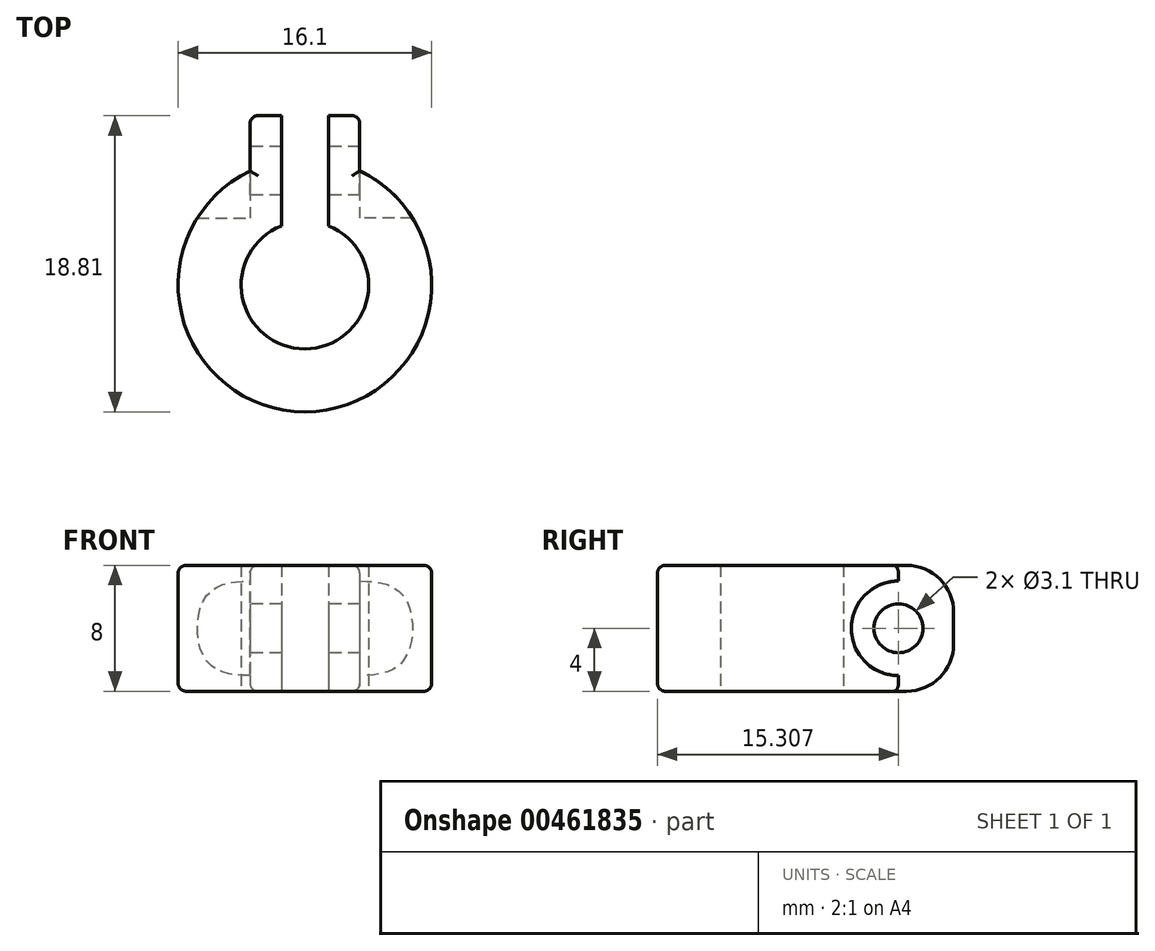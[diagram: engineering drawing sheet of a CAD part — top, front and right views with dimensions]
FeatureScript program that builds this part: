
annotation { "Feature Type Name" : "Feature", "Feature Type Description" : "" }
export const myFeature = defineFeature(function(context is Context, id is Id, definition is map)
    precondition{}
    {
        {
            var Q0;
            Q0=qCreatedBy(makeId("Top.planeOp"),FACE);
            var sketch = newSketch(context, id + "F0", { "sketchPlane" : qUnion([Q0])});
            skArc(sketch, "E0", {"start": v(-1.5, 3.76) * mm, "mid": v(0, -4.05) * mm, "end": v(1.5, 3.76) * mm});
            skArc(sketch, "E1.0", {"start": v(-3.48, 7.26) * mm, "mid": v(0, -8.05) * mm, "end": v(3.48, 7.26) * mm});
            skLineSegment(sketch, "E2.left", {"start": v(1.5, 7.9) * mm, "end": v(1.5, 3.76) * mm});
            skLineSegment(sketch, "E2.right", {"start": v(-1.5, 7.9) * mm, "end": v(-1.5, 3.76) * mm});
            skLineSegment(sketch, "E3.top", {"start": v(-1.5, 9.76) * mm, "end": v(-3.48, 9.76) * mm});
            skLineSegment(sketch, "E3.left", {"start": v(-1.5, 3.76) * mm, "end": v(-1.5, 9.76) * mm});
            skLineSegment(sketch, "E3.right", {"start": v(-3.48, 7.26) * mm, "end": v(-3.48, 9.76) * mm});
            skLineSegment(sketch, "E4.MirrorCS", {"start": v(1.5, 9.76) * mm, "end": v(3.48, 9.76) * mm});
            skLineSegment(sketch, "E5.MirrorCS", {"start": v(3.48, 7.26) * mm, "end": v(3.48, 9.76) * mm});
            skLineSegment(sketch, "E6.MirrorCS", {"start": v(1.5, 3.76) * mm, "end": v(1.5, 9.76) * mm});
            skSolve(sketch);
        }
        {
            var Q0;
            Q0=qSketchRegion(id+"F0",true);
            extrude(context, id + "F1", {"entities" : qUnion([Q0]), "depth" : 8 * mm});
        }
        {
            var Q0;
            Q0=qCreatedBy(makeId("Right.planeOp"),FACE);
            var sketch = newSketch(context, id + "F2", { "sketchPlane" : qUnion([Q0])});
            skCircle(sketch, "E7", {"center": v(7.26, 4) * mm, "radius": 1.55 * mm});
            skSolve(sketch);
        }
        {
            var Q0;
            Q0=qSketchRegion(id+"F2",true);
            extrude(context, id + "F3", {"entities" : qUnion([Q0]), "operationType" : NewBodyOperationType.REMOVE, "endBound" : BoundingType.SYMMETRIC, "depth" : 25 * mm});
        }
        {
            var Q0;
            Q0=makeQuery(id+"F1.opExtrude","SWEPT_FACE",FACE,{"disambiguationData":[OSD([sQuery(id+"F0.wireOp",EDGE,"E4.MirrorCS")])]});
            var Q1;
            Q1=makeQuery(id+"F1.opExtrude","SWEPT_FACE",FACE,{"disambiguationData":[OSD([sQuery(id+"F0.wireOp",EDGE,"E3.top")])]});
            extrude(context, id + "F4", {"entities" : qUnion([Q0, Q1]), "operationType" : NewBodyOperationType.ADD, "depth" : 1 * mm});
        }
        {
            var Q0;
            {var subQ0=sQuery(id+"F0.wireOp",EDGE,"E5.MirrorCS");Q0=makeQuery(id+"F4.boolean.opBoolean","MERGE",FACE,{"derivedFrom":[makeQuery(id+"F1.opExtrude","SWEPT_FACE",FACE,{"disambiguationData":[OSD([subQ0])]}),makeQuery(id+"F4.opExtrude","SWEPT_FACE",FACE,{"disambiguationData":[OSD([sQuery(id+"F0.wireOp",EDGE,"E4.MirrorCS"),subQ0])]})]});}
            var sketch = newSketch(context, id + "F5", { "sketchPlane" : qUnion([Q0])});
            skPoint(sketch, "E8.0", {"position": v(7.26, 4) * mm});
            skCircle(sketch, "E9", {"center": v(7.26, 4) * mm, "radius": 3 * mm});
            skSolve(sketch);
        }
        {
            var Q0;
            {var subQ2=sQuery(id+"F0.wireOp",EDGE,"E5.MirrorCS");var subQ9=makeQuery(id+"F3.opExtrude","SWEPT_FACE",FACE,{"disambiguationData":[OSD([sQuery(id+"F2.wireOp",EDGE,"E7")])]});var subQ11=makeQuery(id+"F1.opExtrude","SWEPT_FACE",FACE,{"disambiguationData":[OSD([subQ2])]});var subQ17=makeQuery(id+"F3.boolean.opBoolean","INTERSECT",EDGE,{"derivedFrom":[subQ11,subQ9]});Q0=makeQuery(id+"F5.imprint","IMPRINT",FACE,{"disambiguationData":[TD([[makeQuery(id+"F5.imprint","IMPRINT",EDGE,{"derivedFrom":subQ17}),1.0]])]});}
            extrude(context, id + "F6", {"entities" : qUnion([Q0]), "operationType" : NewBodyOperationType.REMOVE, "depth" : 25 * mm});
        }
        {
            var Q0;
            {var subQ0=sQuery(id+"F0.wireOp",EDGE,"E3.right");Q0=makeQuery(id+"F4.boolean.opBoolean","MERGE",FACE,{"derivedFrom":[makeQuery(id+"F1.opExtrude","SWEPT_FACE",FACE,{"disambiguationData":[OSD([subQ0])]}),makeQuery(id+"F4.opExtrude","SWEPT_FACE",FACE,{"disambiguationData":[OSD([sQuery(id+"F0.wireOp",EDGE,"E3.top"),subQ0])]})]});}
            var sketch = newSketch(context, id + "F7", { "sketchPlane" : qUnion([Q0])});
            skPoint(sketch, "E10.0", {"position": v(-7.26, 4) * mm});
            skCircle(sketch, "E11", {"center": v(-7.26, 4) * mm, "radius": 3 * mm});
            skSolve(sketch);
        }
        {
            var Q0;
            {var subQ4=sQuery(id+"F0.wireOp",EDGE,"E3.right");var subQ9=makeQuery(id+"F3.opExtrude","SWEPT_FACE",FACE,{"disambiguationData":[OSD([sQuery(id+"F2.wireOp",EDGE,"E7")])]});var subQ11=makeQuery(id+"F1.opExtrude","SWEPT_FACE",FACE,{"disambiguationData":[OSD([subQ4])]});var subQ17=makeQuery(id+"F3.boolean.opBoolean","INTERSECT",EDGE,{"derivedFrom":[subQ11,subQ9]});Q0=makeQuery(id+"F7.imprint","IMPRINT",FACE,{"disambiguationData":[TD([[makeQuery(id+"F7.imprint","IMPRINT",EDGE,{"derivedFrom":subQ17}),-1.0]])]});}
            extrude(context, id + "F8", {"entities" : qUnion([Q0]), "operationType" : NewBodyOperationType.REMOVE, "depth" : 25 * mm});
        }
        {
            var Q0;
            {var subQ0=sQuery(id+"F0.wireOp",EDGE,"E4.MirrorCS");Q0=makeQuery(id+"F4.opExtrude","CAP_EDGE",EDGE,{"disambiguationData":[OSD([subQ0]),TDD([makeQuery(id+"F1.opExtrude","CAP_EDGE",EDGE,{"disambiguationData":[OSD([subQ0])],"isStart":false})])],"isStart":false});}
            var Q1;
            {var subQ0=sQuery(id+"F0.wireOp",EDGE,"E4.MirrorCS");Q1=makeQuery(id+"F4.opExtrude","CAP_EDGE",EDGE,{"disambiguationData":[OSD([subQ0]),TDD([makeQuery(id+"F1.opExtrude","CAP_EDGE",EDGE,{"disambiguationData":[OSD([subQ0])],"isStart":true})])],"isStart":false});}
            fillet(context, id + "F9", {"entities" : qUnion([Q0, Q1]), "radius" : 3 * mm, "tangentPropagation" : true, "allowEdgeOverflow" : false});
        }
        {
            var Q0;
            {var subQ0=sQuery(id+"F0.wireOp",EDGE,"E3.top");Q0=makeQuery(id+"F4.opExtrude","CAP_EDGE",EDGE,{"disambiguationData":[OSD([subQ0]),TDD([makeQuery(id+"F1.opExtrude","CAP_EDGE",EDGE,{"disambiguationData":[OSD([subQ0])],"isStart":false})])],"isStart":false});}
            var Q1;
            {var subQ0=sQuery(id+"F0.wireOp",EDGE,"E3.top");Q1=makeQuery(id+"F4.opExtrude","CAP_EDGE",EDGE,{"disambiguationData":[OSD([subQ0]),TDD([makeQuery(id+"F1.opExtrude","CAP_EDGE",EDGE,{"disambiguationData":[OSD([subQ0])],"isStart":true})])],"isStart":false});}
            fillet(context, id + "F10", {"entities" : qUnion([Q0, Q1]), "radius" : 3 * mm, "tangentPropagation" : true, "allowEdgeOverflow" : false});
        }
        {
            var Q0;
            {var subQ0=sQuery(id+"F0.wireOp",EDGE,"E3.right");var subQ1=sQuery(id+"F0.wireOp",EDGE,"E3.top");Q0=makeQuery(id+"F10.opFillet","BLEND_EDGE",EDGE,{"blendedFrom":[makeQuery(id+"F4.opExtrude","CAP_EDGE",EDGE,{"disambiguationData":[OSD([subQ1]),TDD([makeQuery(id+"F1.opExtrude","CAP_EDGE",EDGE,{"disambiguationData":[OSD([subQ1])],"isStart":false})])],"isStart":false}),makeQuery(id+"F8.boolean.opBoolean","MERGE",FACE,{"derivedFrom":[makeQuery(id+"F4.boolean.opBoolean","MERGE",FACE,{"derivedFrom":[makeQuery(id+"F1.opExtrude","SWEPT_FACE",FACE,{"disambiguationData":[OSD([subQ0])]}),makeQuery(id+"F4.opExtrude","SWEPT_FACE",FACE,{"disambiguationData":[OSD([subQ1,subQ0])]})]}),makeQuery(id+"F8.opExtrude","CAP_FACE",FACE,{"disambiguationData":[OSD([sQuery(id+"F0.wireOp",EDGE,"E1.0"),subQ0,sQuery(id+"F2.wireOp",EDGE,"E7"),sQuery(id+"F7.wireOp",EDGE,"E11")])],"isStart":true})]})],"blendedInto":[makeQuery(id+"F8.boolean.opBoolean","MERGE",FACE,{"derivedFrom":[makeQuery(id+"F4.boolean.opBoolean","MERGE",FACE,{"derivedFrom":[makeQuery(id+"F1.opExtrude","SWEPT_FACE",FACE,{"disambiguationData":[OSD([subQ0])]}),makeQuery(id+"F4.opExtrude","SWEPT_FACE",FACE,{"disambiguationData":[OSD([subQ1,subQ0])]})]}),makeQuery(id+"F8.opExtrude","CAP_FACE",FACE,{"disambiguationData":[OSD([sQuery(id+"F0.wireOp",EDGE,"E1.0"),subQ0,sQuery(id+"F2.wireOp",EDGE,"E7"),sQuery(id+"F7.wireOp",EDGE,"E11")])],"isStart":true})]})]});}
            var Q1;
            {var subQ0=sQuery(id+"F0.wireOp",EDGE,"E3.right");var subQ1=sQuery(id+"F0.wireOp",EDGE,"E3.top");Q1=makeQuery(id+"F4.boolean.opBoolean","MERGE",EDGE,{"derivedFrom":[makeQuery(id+"F1.opExtrude","CAP_EDGE",EDGE,{"disambiguationData":[OSD([subQ0])],"isStart":false}),makeQuery(id+"F4.opExtrude","SWEPT_EDGE",EDGE,{"disambiguationData":[OSD([subQ1,subQ0]),TDD([makeQuery(id+"F1.opExtrude","CAP_VERTEX",VERTEX,{"disambiguationData":[OSD([subQ1,subQ0])],"isStart":false})])]})]});}
            var Q2;
            Q2=makeQuery(id+"F1.opExtrude","CAP_EDGE",EDGE,{"disambiguationData":[OSD([sQuery(id+"F0.wireOp",EDGE,"E1.0")])],"isStart":false});
            var Q3;
            {var subQ0=sQuery(id+"F0.wireOp",EDGE,"E5.MirrorCS");var subQ1=sQuery(id+"F0.wireOp",EDGE,"E4.MirrorCS");Q3=makeQuery(id+"F4.boolean.opBoolean","MERGE",EDGE,{"derivedFrom":[makeQuery(id+"F1.opExtrude","CAP_EDGE",EDGE,{"disambiguationData":[OSD([subQ0])],"isStart":false}),makeQuery(id+"F4.opExtrude","SWEPT_EDGE",EDGE,{"disambiguationData":[OSD([subQ1,subQ0]),TDD([makeQuery(id+"F1.opExtrude","CAP_VERTEX",VERTEX,{"disambiguationData":[OSD([subQ1,subQ0])],"isStart":false})])]})]});}
            var Q4;
            {var subQ0=sQuery(id+"F0.wireOp",EDGE,"E5.MirrorCS");var subQ1=sQuery(id+"F0.wireOp",EDGE,"E4.MirrorCS");Q4=makeQuery(id+"F9.opFillet","BLEND_EDGE",EDGE,{"blendedFrom":[makeQuery(id+"F4.opExtrude","CAP_EDGE",EDGE,{"disambiguationData":[OSD([subQ1]),TDD([makeQuery(id+"F1.opExtrude","CAP_EDGE",EDGE,{"disambiguationData":[OSD([subQ1])],"isStart":false})])],"isStart":false}),makeQuery(id+"F6.boolean.opBoolean","MERGE",FACE,{"derivedFrom":[makeQuery(id+"F4.boolean.opBoolean","MERGE",FACE,{"derivedFrom":[makeQuery(id+"F1.opExtrude","SWEPT_FACE",FACE,{"disambiguationData":[OSD([subQ0])]}),makeQuery(id+"F4.opExtrude","SWEPT_FACE",FACE,{"disambiguationData":[OSD([subQ1,subQ0])]})]}),makeQuery(id+"F6.opExtrude","CAP_FACE",FACE,{"disambiguationData":[OSD([sQuery(id+"F0.wireOp",EDGE,"E1.0"),subQ0,sQuery(id+"F2.wireOp",EDGE,"E7"),sQuery(id+"F5.wireOp",EDGE,"E9")])],"isStart":true})]})],"blendedInto":[makeQuery(id+"F6.boolean.opBoolean","MERGE",FACE,{"derivedFrom":[makeQuery(id+"F4.boolean.opBoolean","MERGE",FACE,{"derivedFrom":[makeQuery(id+"F1.opExtrude","SWEPT_FACE",FACE,{"disambiguationData":[OSD([subQ0])]}),makeQuery(id+"F4.opExtrude","SWEPT_FACE",FACE,{"disambiguationData":[OSD([subQ1,subQ0])]})]}),makeQuery(id+"F6.opExtrude","CAP_FACE",FACE,{"disambiguationData":[OSD([sQuery(id+"F0.wireOp",EDGE,"E1.0"),subQ0,sQuery(id+"F2.wireOp",EDGE,"E7"),sQuery(id+"F5.wireOp",EDGE,"E9")])],"isStart":true})]})]});}
            var Q5;
            Q5=makeQuery(id+"F4.opExtrude","CAP_EDGE",EDGE,{"disambiguationData":[OSD([sQuery(id+"F0.wireOp",EDGE,"E4.MirrorCS"),sQuery(id+"F0.wireOp",EDGE,"E5.MirrorCS")])],"isStart":false});
            var Q6;
            Q6=makeQuery(id+"F4.opExtrude","CAP_EDGE",EDGE,{"disambiguationData":[OSD([sQuery(id+"F0.wireOp",EDGE,"E3.top"),sQuery(id+"F0.wireOp",EDGE,"E3.right")])],"isStart":false});
            var Q7;
            {var subQ0=sQuery(id+"F0.wireOp",EDGE,"E3.right");var subQ1=sQuery(id+"F0.wireOp",EDGE,"E3.top");Q7=makeQuery(id+"F10.opFillet","BLEND_EDGE",EDGE,{"blendedFrom":[makeQuery(id+"F4.opExtrude","CAP_EDGE",EDGE,{"disambiguationData":[OSD([subQ1]),TDD([makeQuery(id+"F1.opExtrude","CAP_EDGE",EDGE,{"disambiguationData":[OSD([subQ1])],"isStart":true})])],"isStart":false}),makeQuery(id+"F8.boolean.opBoolean","MERGE",FACE,{"derivedFrom":[makeQuery(id+"F4.boolean.opBoolean","MERGE",FACE,{"derivedFrom":[makeQuery(id+"F1.opExtrude","SWEPT_FACE",FACE,{"disambiguationData":[OSD([subQ0])]}),makeQuery(id+"F4.opExtrude","SWEPT_FACE",FACE,{"disambiguationData":[OSD([subQ1,subQ0])]})]}),makeQuery(id+"F8.opExtrude","CAP_FACE",FACE,{"disambiguationData":[OSD([sQuery(id+"F0.wireOp",EDGE,"E1.0"),subQ0,sQuery(id+"F2.wireOp",EDGE,"E7"),sQuery(id+"F7.wireOp",EDGE,"E11")])],"isStart":true})]})],"blendedInto":[makeQuery(id+"F8.boolean.opBoolean","MERGE",FACE,{"derivedFrom":[makeQuery(id+"F4.boolean.opBoolean","MERGE",FACE,{"derivedFrom":[makeQuery(id+"F1.opExtrude","SWEPT_FACE",FACE,{"disambiguationData":[OSD([subQ0])]}),makeQuery(id+"F4.opExtrude","SWEPT_FACE",FACE,{"disambiguationData":[OSD([subQ1,subQ0])]})]}),makeQuery(id+"F8.opExtrude","CAP_FACE",FACE,{"disambiguationData":[OSD([sQuery(id+"F0.wireOp",EDGE,"E1.0"),subQ0,sQuery(id+"F2.wireOp",EDGE,"E7"),sQuery(id+"F7.wireOp",EDGE,"E11")])],"isStart":true})]})]});}
            var Q8;
            {var subQ0=sQuery(id+"F0.wireOp",EDGE,"E3.right");var subQ1=sQuery(id+"F0.wireOp",EDGE,"E3.top");Q8=makeQuery(id+"F4.boolean.opBoolean","MERGE",EDGE,{"derivedFrom":[makeQuery(id+"F1.opExtrude","CAP_EDGE",EDGE,{"disambiguationData":[OSD([subQ0])],"isStart":true}),makeQuery(id+"F4.opExtrude","SWEPT_EDGE",EDGE,{"disambiguationData":[OSD([subQ1,subQ0]),TDD([makeQuery(id+"F1.opExtrude","CAP_VERTEX",VERTEX,{"disambiguationData":[OSD([subQ1,subQ0])],"isStart":true})])]})]});}
            var Q9;
            Q9=makeQuery(id+"F1.opExtrude","CAP_EDGE",EDGE,{"disambiguationData":[OSD([sQuery(id+"F0.wireOp",EDGE,"E1.0")])],"isStart":true});
            var Q10;
            {var subQ0=sQuery(id+"F0.wireOp",EDGE,"E5.MirrorCS");var subQ1=sQuery(id+"F0.wireOp",EDGE,"E4.MirrorCS");Q10=makeQuery(id+"F4.boolean.opBoolean","MERGE",EDGE,{"derivedFrom":[makeQuery(id+"F1.opExtrude","CAP_EDGE",EDGE,{"disambiguationData":[OSD([subQ0])],"isStart":true}),makeQuery(id+"F4.opExtrude","SWEPT_EDGE",EDGE,{"disambiguationData":[OSD([subQ1,subQ0]),TDD([makeQuery(id+"F1.opExtrude","CAP_VERTEX",VERTEX,{"disambiguationData":[OSD([subQ1,subQ0])],"isStart":true})])]})]});}
            var Q11;
            {var subQ0=sQuery(id+"F0.wireOp",EDGE,"E5.MirrorCS");var subQ1=sQuery(id+"F0.wireOp",EDGE,"E4.MirrorCS");Q11=makeQuery(id+"F9.opFillet","BLEND_EDGE",EDGE,{"blendedFrom":[makeQuery(id+"F4.opExtrude","CAP_EDGE",EDGE,{"disambiguationData":[OSD([subQ1]),TDD([makeQuery(id+"F1.opExtrude","CAP_EDGE",EDGE,{"disambiguationData":[OSD([subQ1])],"isStart":true})])],"isStart":false}),makeQuery(id+"F6.boolean.opBoolean","MERGE",FACE,{"derivedFrom":[makeQuery(id+"F4.boolean.opBoolean","MERGE",FACE,{"derivedFrom":[makeQuery(id+"F1.opExtrude","SWEPT_FACE",FACE,{"disambiguationData":[OSD([subQ0])]}),makeQuery(id+"F4.opExtrude","SWEPT_FACE",FACE,{"disambiguationData":[OSD([subQ1,subQ0])]})]}),makeQuery(id+"F6.opExtrude","CAP_FACE",FACE,{"disambiguationData":[OSD([sQuery(id+"F0.wireOp",EDGE,"E1.0"),subQ0,sQuery(id+"F2.wireOp",EDGE,"E7"),sQuery(id+"F5.wireOp",EDGE,"E9")])],"isStart":true})]})],"blendedInto":[makeQuery(id+"F6.boolean.opBoolean","MERGE",FACE,{"derivedFrom":[makeQuery(id+"F4.boolean.opBoolean","MERGE",FACE,{"derivedFrom":[makeQuery(id+"F1.opExtrude","SWEPT_FACE",FACE,{"disambiguationData":[OSD([subQ0])]}),makeQuery(id+"F4.opExtrude","SWEPT_FACE",FACE,{"disambiguationData":[OSD([subQ1,subQ0])]})]}),makeQuery(id+"F6.opExtrude","CAP_FACE",FACE,{"disambiguationData":[OSD([sQuery(id+"F0.wireOp",EDGE,"E1.0"),subQ0,sQuery(id+"F2.wireOp",EDGE,"E7"),sQuery(id+"F5.wireOp",EDGE,"E9")])],"isStart":true})]})]});}
            fillet(context, id + "F11", {"entities" : qUnion([Q0, Q1, Q2, Q3, Q4, Q5, Q6, Q7, Q8, Q9, Q10, Q11]), "radius" : 0.5 * mm, "tangentPropagation" : true, "allowEdgeOverflow" : false});
        }
    });
